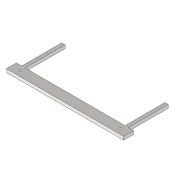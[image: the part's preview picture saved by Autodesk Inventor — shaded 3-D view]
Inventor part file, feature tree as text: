
AUTODESK INVENTOR PART (.ipt)
format: ipt  version: 2020 (Build 240168000, 168)  size: 112,640 bytes
history: native  units: mm
features: extrude x3, sketch x3
ambient origin geometry x8: Origin, YZ Plane, XZ Plane, XY Plane, X Axis, Y Axis, Z Axis, Center Point
bodies: Volumenkörper1 (feature_tree)
feature tree (6):
  extrude  "Extrusion1"  Depth=600.0mm
  extrude  "Extrusion2"  Depth=1500.0mm
  extrude  "Extrusion3"  Depth=50.0mm TaperAngle=0.0deg
  sketch  "Skizze1"  dims[d0=50.0mm d1=600.0mm]
  sketch  "Skizze2"  dims[d2=150.0mm d3=1500.0mm]
  sketch  "Skizze3"  dims[d4=80.0mm d5=50.0mm d6=0.0mm d7=85.0mm d8=85.0mm d9=1500.0mm d10=75.0mm d11=25.0mm d12=0.0mm d13=35.0mm d14=35.0mm d15=0.0mm d16=0.0mm]
